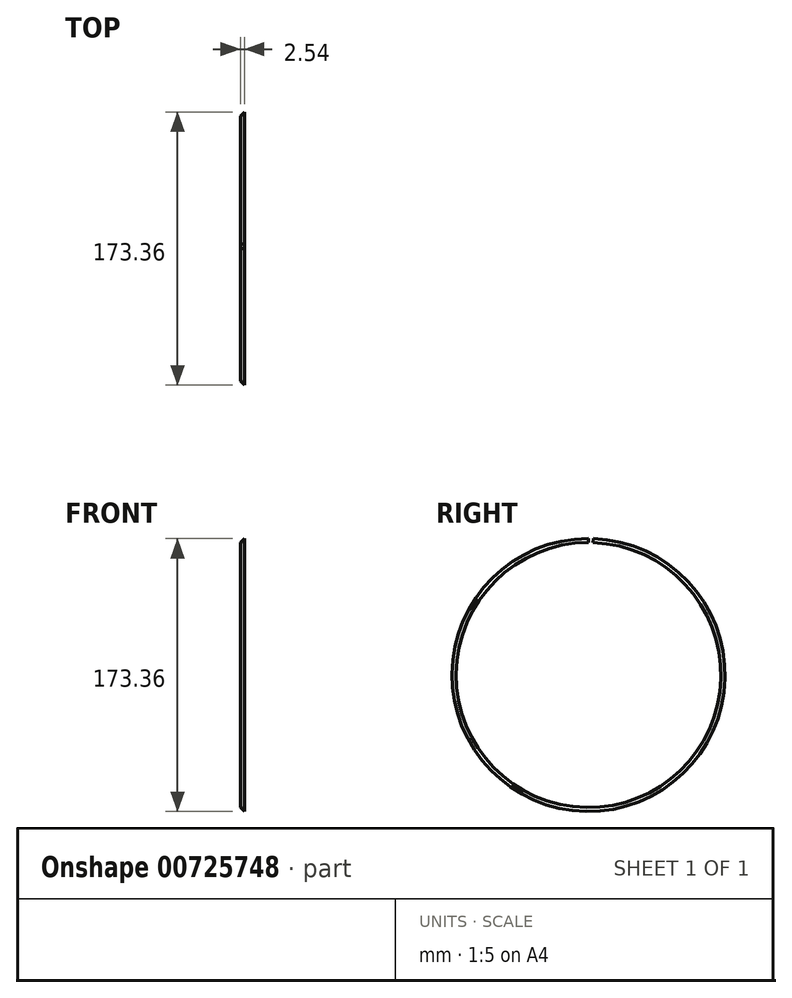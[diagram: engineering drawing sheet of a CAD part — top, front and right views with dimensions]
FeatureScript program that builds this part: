
annotation { "Feature Type Name" : "Feature", "Feature Type Description" : "" }
export const myFeature = defineFeature(function(context is Context, id is Id, definition is map)
    precondition{}
    {
        {
            var Q0;
            Q0=qCreatedBy(makeId("Front.planeOp"),FACE);
            var sketch = newSketch(context, id + "F0", { "sketchPlane" : qUnion([Q0])});
            skLineSegment(sketch, "E0.bottom", {"start": v(-8.9, 86.68) * mm, "end": v(-6.37, 86.68) * mm});
            skLineSegment(sketch, "E0.top", {"start": v(-8.9, 84.14) * mm, "end": v(-6.37, 84.14) * mm});
            skLineSegment(sketch, "E0.left", {"start": v(-8.9, 86.68) * mm, "end": v(-8.9, 84.14) * mm});
            skLineSegment(sketch, "E0.right", {"start": v(-6.37, 86.68) * mm, "end": v(-6.37, 84.14) * mm});
            skSolve(sketch);
        }
        {
            var Q0;
            Q0=qCreatedBy(makeId("Front.planeOp"),FACE);
            var sketch = newSketch(context, id + "F1", { "sketchPlane" : qUnion([Q0])});
            skLineSegment(sketch, "E1", {"start": v(-84.46, 0) * mm, "end": v(95.96, 0) * mm, "construction": true});
            skSolve(sketch);
        }
        {
            var Q0;
            Q0 = qSketchRegion(id + "F0", true);
            var Q1;
            Q1=sQuery(id+"F1.wireOp",EDGE,"E1");
            revolve(context, id + "F2", {"surfaceOperationType" : NewSurfaceOperationType.NEW, "entities" : qUnion([Q0]), "axis" : qUnion([Q1]), "revolveType" : RevolveType.ONE_DIRECTION, "angle" : 358 * degree});
        }
        {
            var Q0;
            Q0=makeQuery(id+"F2.opRevolve","SWEPT_EDGE",EDGE,{"disambiguationData":[OSD([sQuery(id+"F0.wireOp",EDGE,"E0.bottom"),sQuery(id+"F0.wireOp",EDGE,"E0.left")])]});
            chamfer(context, id + "F3", {"entities" : qUnion([Q0]), "width" : 2.54 * mm, "tangentPropagation" : true});
        }
    });
